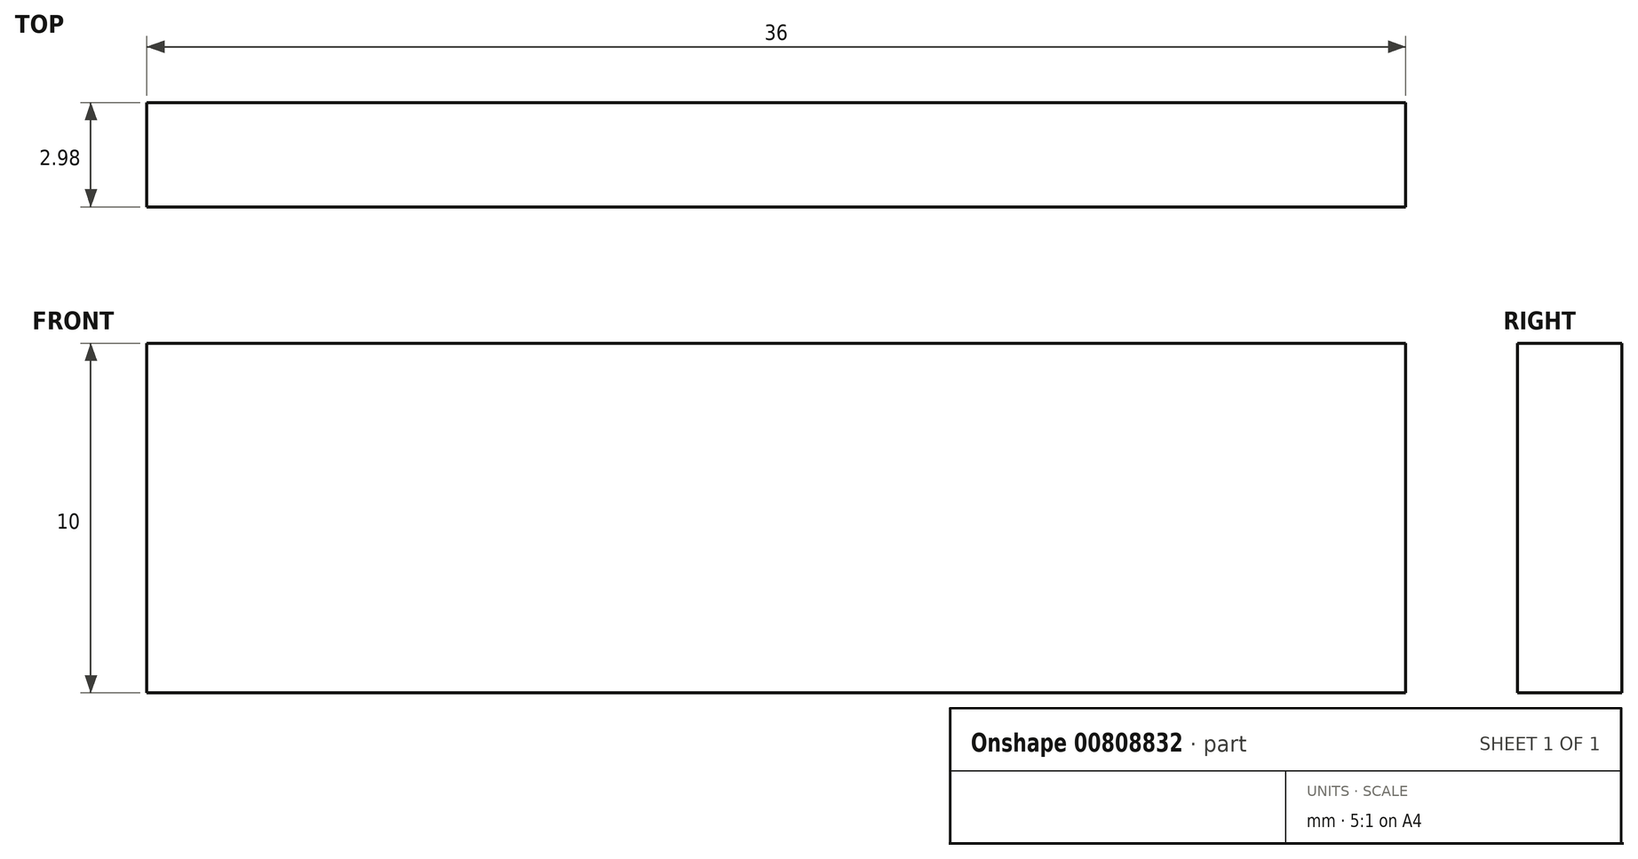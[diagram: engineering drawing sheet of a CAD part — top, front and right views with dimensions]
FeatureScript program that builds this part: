
annotation { "Feature Type Name" : "Feature", "Feature Type Description" : "" }
export const myFeature = defineFeature(function(context is Context, id is Id, definition is map)
    precondition{}
    {
        {
            var Q0;
            Q0=qCreatedBy(makeId("Front.planeOp"),FACE);
            var sketch = newSketch(context, id + "F0", { "sketchPlane" : qUnion([Q0])});
            skLineSegment(sketch, "E0.bottom", {"start": v(-18, 5) * mm, "end": v(18, 5) * mm});
            skLineSegment(sketch, "E0.top", {"start": v(-18, -5) * mm, "end": v(18, -5) * mm});
            skLineSegment(sketch, "E0.left", {"start": v(-18, 5) * mm, "end": v(-18, -5) * mm});
            skLineSegment(sketch, "E0.right", {"start": v(18, 5) * mm, "end": v(18, -5) * mm});
            skPoint(sketch, "E0.middle", {"position": v(0, 0) * mm});
            skSolve(sketch);
        }
        {
            var Q0;
            Q0=qSketchRegion(id+"F0",true);
            extrude(context, id + "F1", {"entities" : qUnion([Q0]), "depth" : 2.98 * mm, "offsetDistance" : 25 * mm});
        }
    });
